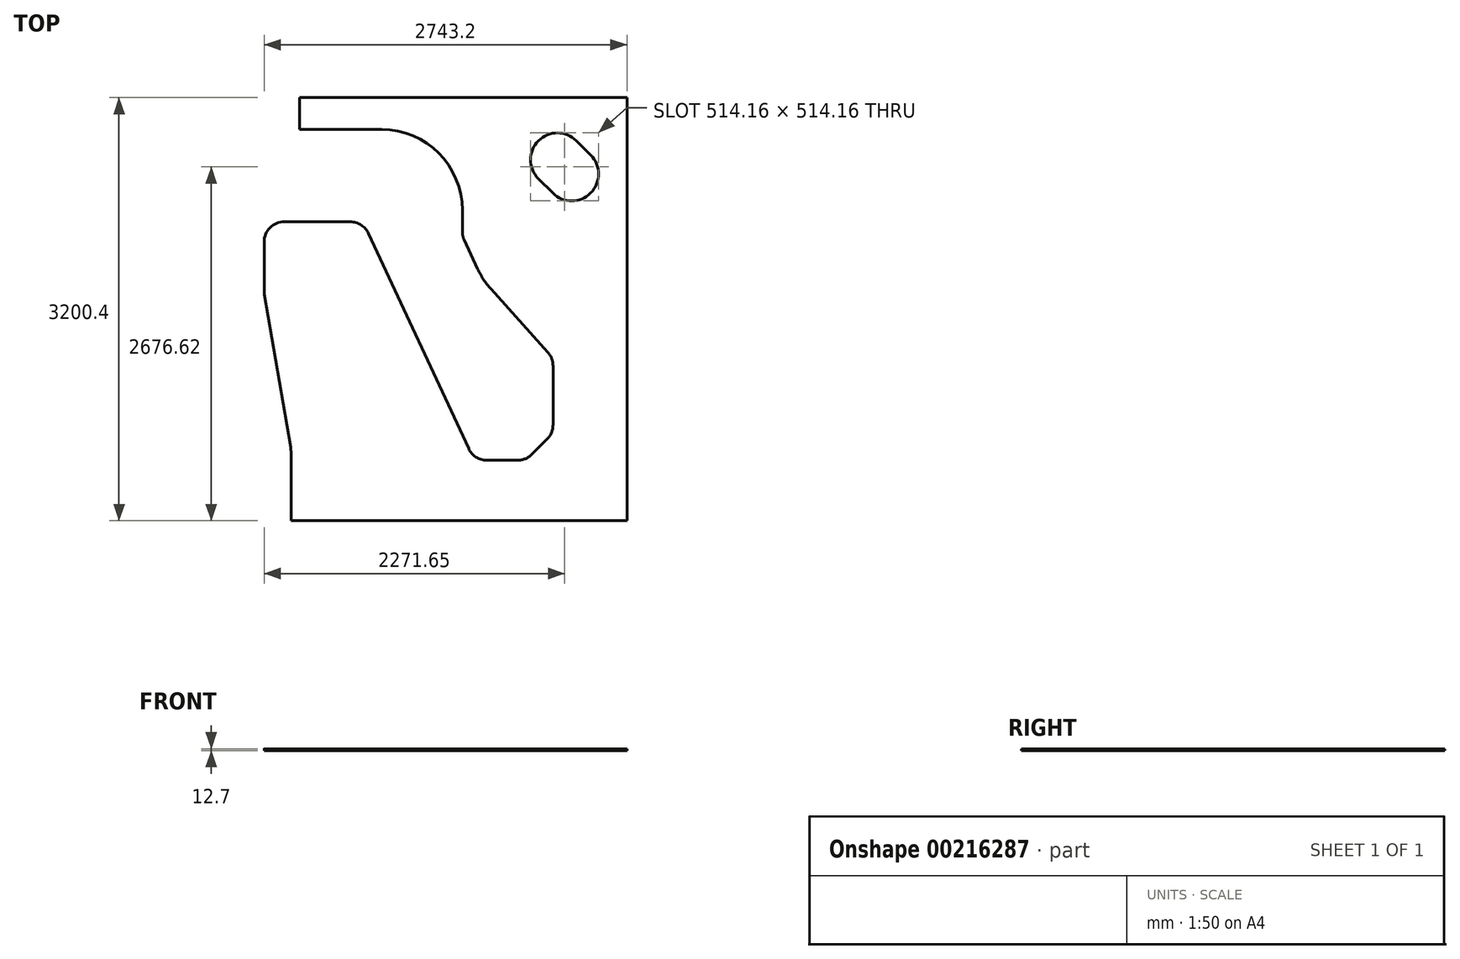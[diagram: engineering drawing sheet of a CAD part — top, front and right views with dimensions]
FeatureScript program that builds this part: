
annotation { "Feature Type Name" : "Feature", "Feature Type Description" : "" }
export const myFeature = defineFeature(function(context is Context, id is Id, definition is map)
    precondition{}
    {
        {
            var Q0;
            Q0=qCreatedBy(makeId("Top.planeOp"),FACE);
            var sketch = newSketch(context, id + "F0", { "sketchPlane" : qUnion([Q0])});
            skArc(sketch, "E0", {"start": v(-5251.06, 895.22) * mm, "mid": v(-5538.43, 895.22) * mm, "end": v(-5538.43, 607.85) * mm});
            skArc(sketch, "E1", {"start": v(-5430.67, 500.08) * mm, "mid": v(-5143.3, 500.08) * mm, "end": v(-5143.3, 787.45) * mm});
            skLineSegment(sketch, "E2", {"start": v(-5251.06, 895.22) * mm, "end": v(-5143.3, 787.45) * mm});
            skLineSegment(sketch, "E3", {"start": v(-5538.43, 607.85) * mm, "end": v(-5430.67, 500.08) * mm});
            skLineSegment(sketch, "E4", {"start": v(-8374.52, 1221.43) * mm, "end": v(-7345.82, 1221.43) * mm});
            skLineSegment(sketch, "E5", {"start": v(-7409.32, -1978.97) * mm, "end": v(-4869.32, -1978.97) * mm});
            skLineSegment(sketch, "E6", {"start": v(-7409.32, -1449.55) * mm, "end": v(-7409.32, -1978.97) * mm});
            skLineSegment(sketch, "E7", {"start": v(-7345.82, 980.13) * mm, "end": v(-8374.52, 980.13) * mm});
            skLineSegment(sketch, "E8", {"start": v(-8374.52, 992.83) * mm, "end": v(-8374.52, 1221.43) * mm});
            skLineSegment(sketch, "E9", {"start": v(-7345.82, 980.13) * mm, "end": v(-6723.52, 980.13) * mm});
            skLineSegment(sketch, "E10", {"start": v(-7345.82, 980.13) * mm, "end": v(-7345.82, 1221.43) * mm});
            skLineSegment(sketch, "E11", {"start": v(-5467.14, -705.4) * mm, "end": v(-5897.87, -225.9) * mm});
            skLineSegment(sketch, "E12", {"start": v(-4869.32, -1978.97) * mm, "end": v(-4869.32, 1221.43) * mm});
            skLineSegment(sketch, "E13", {"start": v(-7345.82, 1221.43) * mm, "end": v(-4869.32, 1221.43) * mm});
            skLineSegment(sketch, "E14", {"start": v(-7460.12, 281.63) * mm, "end": v(-6960.57, 281.63) * mm});
            skLineSegment(sketch, "E15", {"start": v(-5587.74, -1477.13) * mm, "end": v(-5472.75, -1362.15) * mm});
            skLineSegment(sketch, "E16", {"start": v(-5928.07, -1521.77) * mm, "end": v(-5695.5, -1521.77) * mm});
            skArc(sketch, "E17", {"start": v(-5695.5, -1521.77) * mm, "mid": v(-5637.18, -1510.17) * mm, "end": v(-5587.74, -1477.13) * mm});
            skLineSegment(sketch, "E18", {"start": v(-5428.12, -807.23) * mm, "end": v(-5428.12, -1254.38) * mm});
            skArc(sketch, "E19", {"start": v(-5428.12, -807.23) * mm, "mid": v(-5438.2, -752.7) * mm, "end": v(-5467.14, -705.4) * mm});
            skArc(sketch, "E20", {"start": v(-5472.75, -1362.15) * mm, "mid": v(-5439.72, -1312.7) * mm, "end": v(-5428.12, -1254.38) * mm});
            skLineSegment(sketch, "E21", {"start": v(-6822.36, 193.46) * mm, "end": v(-6066.27, -1433.6) * mm});
            skArc(sketch, "E22", {"start": v(-6066.27, -1433.6) * mm, "mid": v(-6010.04, -1497.85) * mm, "end": v(-5928.07, -1521.77) * mm});
            skArc(sketch, "E23", {"start": v(-6822.36, 193.46) * mm, "mid": v(-6878.6, 257.71) * mm, "end": v(-6960.57, 281.63) * mm});
            skLineSegment(sketch, "E24", {"start": v(-6113.92, 209.42) * mm, "end": v(-6113.92, 370.53) * mm});
            skLineSegment(sketch, "E25", {"start": v(-6099.72, 145.2) * mm, "end": v(-5997.2, -75.42) * mm});
            skArc(sketch, "E26", {"start": v(-6113.92, 209.42) * mm, "mid": v(-6110.33, 176.53) * mm, "end": v(-6099.72, 145.2) * mm});
            skArc(sketch, "E27", {"start": v(-5997.2, -75.42) * mm, "mid": v(-5953.13, -154.35) * mm, "end": v(-5897.87, -225.9) * mm});
            skArc(sketch, "E28", {"start": v(-6113.92, 370.53) * mm, "mid": v(-6292.46, 801.58) * mm, "end": v(-6723.52, 980.13) * mm});
            skLineSegment(sketch, "E29", {"start": v(-7612.52, -242.32) * mm, "end": v(-7612.52, 129.23) * mm});
            skArc(sketch, "E30", {"start": v(-7460.12, 281.63) * mm, "mid": v(-7567.88, 237) * mm, "end": v(-7612.52, 129.23) * mm});
            skLineSegment(sketch, "E31", {"start": v(-7411.52, -1423.72) * mm, "end": v(-7610.3, -268.16) * mm});
            skArc(sketch, "E32", {"start": v(-7409.32, -1449.55) * mm, "mid": v(-7409.87, -1436.59) * mm, "end": v(-7411.52, -1423.72) * mm});
            skArc(sketch, "E33", {"start": v(-7612.52, -242.32) * mm, "mid": v(-7611.96, -255.29) * mm, "end": v(-7610.3, -268.16) * mm});
            skLineSegment(sketch, "E34", {"start": v(-8374.52, 980.13) * mm, "end": v(-8374.52, 1221.43) * mm});
            skSolve(sketch);
        }
        {
            var Q0;
            Q0=makeQuery(id+"F0.imprint","IMPRINT",FACE,{"disambiguationData":[TD([[makeQuery(id+"F0.imprint","IMPRINT",EDGE,{"derivedFrom":sQuery(id+"F0.wireOp",EDGE,"E0")}),-1.0]])]});
            extrude(context, id + "F1", {"entities" : qUnion([Q0]), "depth" : 12.7 * mm});
        }
    });
